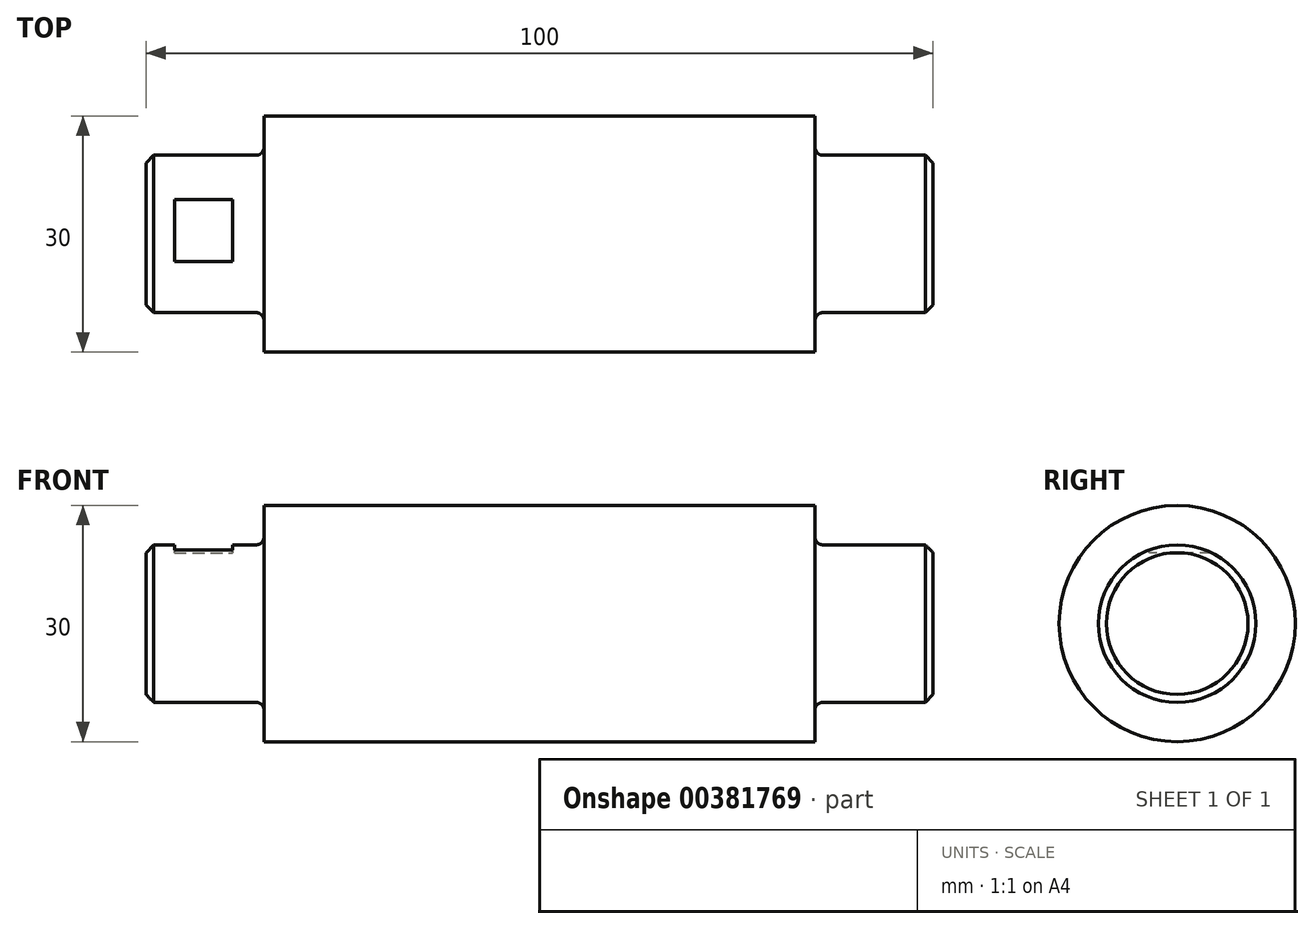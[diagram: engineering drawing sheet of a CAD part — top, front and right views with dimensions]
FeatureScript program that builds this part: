
annotation { "Feature Type Name" : "Feature", "Feature Type Description" : "" }
export const myFeature = defineFeature(function(context is Context, id is Id, definition is map)
    precondition{}
    {
        {
            var Q0;
            Q0=qCreatedBy(makeId("Front.planeOp"),FACE);
            var sketch = newSketch(context, id + "F0", { "sketchPlane" : qUnion([Q0])});
            skLineSegment(sketch, "E0", {"start": v(-50, 0) * mm, "end": v(-50, 10) * mm});
            skLineSegment(sketch, "E1", {"start": v(-50, 10) * mm, "end": v(-35, 10) * mm});
            skLineSegment(sketch, "E2", {"start": v(-35, 10) * mm, "end": v(-35, 15) * mm});
            skLineSegment(sketch, "E3", {"start": v(-35, 15) * mm, "end": v(35, 15) * mm});
            skLineSegment(sketch, "E4", {"start": v(35, 15) * mm, "end": v(35, 10) * mm});
            skLineSegment(sketch, "E5", {"start": v(35, 10) * mm, "end": v(50, 10) * mm});
            skLineSegment(sketch, "E6", {"start": v(50, 10) * mm, "end": v(50, 0) * mm});
            skLineSegment(sketch, "E7", {"start": v(50, 0) * mm, "end": v(-50, 0) * mm});
            skSolve(sketch);
        }
        {
            var Q0;
            Q0=makeQuery(id+"F0.imprint","IMPRINT",FACE,{"disambiguationData":[TD([[makeQuery(id+"F0.imprint","IMPRINT",EDGE,{"derivedFrom":sQuery(id+"F0.wireOp",EDGE,"E0")}),-1.0]])]});
            var Q1;
            Q1=sQuery(id+"F0.wireOp",EDGE,"E7");
            revolve(context, id + "F1", {"entities" : qUnion([Q0]), "axis" : qUnion([Q1]), "revolveType" : RevolveType.FULL});
        }
        {
            var Q0;
            Q0=makeQuery(id+"F1.opRevolve","SWEPT_EDGE",EDGE,{"disambiguationData":[OSD([sQuery(id+"F0.wireOp",EDGE,"E0"),sQuery(id+"F0.wireOp",EDGE,"E1")])]});
            var Q1;
            Q1=makeQuery(id+"F1.opRevolve","SWEPT_EDGE",EDGE,{"disambiguationData":[OSD([sQuery(id+"F0.wireOp",EDGE,"E5"),sQuery(id+"F0.wireOp",EDGE,"E6")])]});
            chamfer(context, id + "F2", {"entities" : qUnion([Q0, Q1]), "width" : 1 * mm, "tangentPropagation" : true});
        }
        {
            var Q0;
            Q0=makeQuery(id+"F1.opRevolve","SWEPT_EDGE",EDGE,{"disambiguationData":[OSD([sQuery(id+"F0.wireOp",EDGE,"E1"),sQuery(id+"F0.wireOp",EDGE,"E2")])]});
            var Q1;
            Q1=makeQuery(id+"F1.opRevolve","SWEPT_EDGE",EDGE,{"disambiguationData":[OSD([sQuery(id+"F0.wireOp",EDGE,"E4"),sQuery(id+"F0.wireOp",EDGE,"E5")])]});
            fillet(context, id + "F3", {"entities" : qUnion([Q0, Q1]), "radius" : 1 * mm, "tangentPropagation" : true, "allowEdgeOverflow" : false});
        }
        {
            var Q0;
            Q0=qCreatedBy(makeId("Top.planeOp"),FACE);
            cPlane(context, id + "F4", {"entities" : qUnion([Q0]), "cplaneType" : CPlaneType.OFFSET, "offset" : 10 * mm, "width" : 150 * mm, "height" : 150 * mm});
        }
        {
            var Q0;
            Q0=qCreatedBy(id+"F4.planeOp",FACE);
            var sketch = newSketch(context, id + "F5", { "sketchPlane" : qUnion([Q0])});
            skLineSegment(sketch, "E8", {"start": v(-39, 5.2) * mm, "end": v(-46.37, 5.2) * mm});
            skLineSegment(sketch, "E9", {"start": v(-39, 5.2) * mm, "end": v(-39, -3.5) * mm});
            skLineSegment(sketch, "E10", {"start": v(-39, -3.5) * mm, "end": v(-46.37, -3.5) * mm});
            skLineSegment(sketch, "E11", {"start": v(-46.37, -3.5) * mm, "end": v(-46.37, 5.2) * mm});
            skSolve(sketch);
        }
        {
            var Q0;
            Q0=makeQuery(id+"F5.imprint","IMPRINT",FACE,{"disambiguationData":[TD([[makeQuery(id+"F5.imprint","IMPRINT",EDGE,{"derivedFrom":sQuery(id+"F5.wireOp",EDGE,"E8")}),1.0]])]});
            extrude(context, id + "F6", {"entities" : qUnion([Q0]), "operationType" : NewBodyOperationType.REMOVE, "oppositeDirection" : true, "depth" : 1 * mm});
        }
    });
